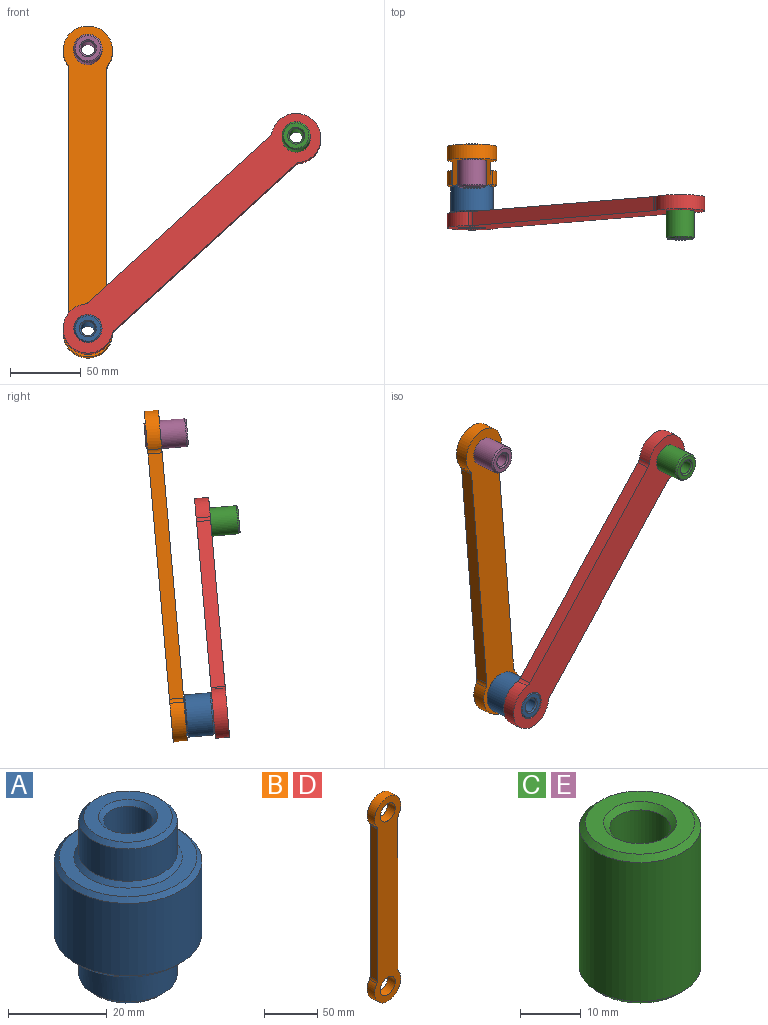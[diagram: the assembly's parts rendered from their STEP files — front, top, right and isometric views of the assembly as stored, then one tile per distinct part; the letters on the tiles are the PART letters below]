
ASSEMBLY  parts=5 mates=4
PART A: 16 faces, bbox 30x30x40 mm
  f0: cylinder r=15mm len=30mm, axis (0,0,-1), area 1696.5mm2, adj f11,f13
  f1: plane 28x28mm, normal (0,0,1), area 235.6mm2, adj f12,f13
  f2: plane 28x28mm, normal (0,0,-1), area 235.6mm2, adj f10,f11
  f3: cylinder r=10mm len=20mm, axis (0,0,-1), area 502.7mm2, adj f12,f15
  f4: plane 18x18mm, normal (0,0,1), area 141.4mm2, adj f14,f15
  f5: cylinder r=10mm len=20mm, axis (0,0,1), area 502.7mm2, adj f9,f10
  f6: plane 18x18mm, normal (0,0,-1), area 141.4mm2, adj f8,f9
  f7: cylinder r=5mm len=38mm, axis (0,0,1), area 1193.8mm2, adj f8,f14
  f8: cone r=6mm half-angle=45deg, axis (0,0,-1), area 48.9mm2, adj f6,f7
  f9: cone r=9mm half-angle=45deg, axis (0,0,1), area 84.4mm2, adj f5,f6
  f10: cone r=10mm half-angle=45deg, axis (0,0,1), area 93.3mm2, adj f2,f5
  f11: cone r=15mm half-angle=45deg, axis (0,0,1), area 128.8mm2, adj f0,f2
  f12: cone r=10mm half-angle=45deg, axis (0,0,-1), area 93.3mm2, adj f1,f3
  f13: cone r=14mm half-angle=45deg, axis (0,0,-1), area 128.8mm2, adj f0,f1
  f14: cone r=5mm half-angle=45deg, axis (0,0,1), area 48.9mm2, adj f4,f7
  f15: cone r=9mm half-angle=45deg, axis (0,0,-1), area 84.4mm2, adj f3,f4
PART B: 12 faces, bbox 35x10x235 mm
  f0: cylinder r=5mm len=10mm, axis (0,1,0), area 30.6mm2, adj f1,f9,f10,f11
  f1: cylinder r=17.5mm len=35mm, axis (0,1,0), area 763.6mm2, adj f0,f2,f10,f11
  f2: cylinder r=5mm len=10mm, axis (0,1,0), area 30.6mm2, adj f1,f3,f10,f11
  f3: plane 174.18x10mm, normal (-1,0,0), area 1741.8mm2, adj f2,f4,f10,f11
  f4: cylinder r=5mm len=10mm, axis (0,1,0), area 30.6mm2, adj f3,f5,f10,f11
  f5: cylinder r=17.5mm len=35mm, axis (0,1,0), area 763.6mm2, adj f4,f6,f10,f11
  f6: cylinder r=5mm len=10mm, axis (0,1,0), area 30.6mm2, adj f5,f9,f10,f11
  f7: cylinder r=10mm len=20mm, axis (0,1,0), area 628.3mm2, adj f10,f11
  f8: cylinder r=10mm len=20mm, axis (0,1,0), area 628.3mm2, adj f10,f11
  f9: plane 174.18x10mm, normal (1,0,0), area 1741.8mm2, adj f0,f6,f10,f11
  f10: plane 235x35mm, normal (0,-1,0), area 5831.3mm2, adj f0,f1,f2,f3,f4,f5,f6,f7
  f11: plane 235x35mm, normal (0,1,0), area 5831.3mm2, adj f0,f1,f2,f3,f4,f5,f6,f7
PART C: 8 faces, bbox 20x20x30 mm
  f0: cylinder r=10mm len=28mm, axis (0,0,-1), area 1759.3mm2, adj f6,f7
  f1: plane 18x18mm, normal (0,0,1), area 141.4mm2, adj f5,f6
  f2: plane 18x18mm, normal (0,0,-1), area 141.4mm2, adj f4,f7
  f3: cylinder r=5mm len=28mm, axis (0,0,-1), area 879.6mm2, adj f4,f5
  f4: cone r=5mm half-angle=45deg, axis (0,0,-1), area 48.9mm2, adj f2,f3
  f5: cone r=6mm half-angle=45deg, axis (0,0,1), area 48.9mm2, adj f1,f3
  f6: cone r=9mm half-angle=45deg, axis (0,0,-1), area 84.4mm2, adj f0,f1
  f7: cone r=10mm half-angle=45deg, axis (0,0,1), area 84.4mm2, adj f0,f2
PART D: same geometry as B
PART E: same geometry as C
PLACE A rot(axis=(-1,0,0),95deg) t=(48.86,-32.99,-9.76)mm
PLACE B rot(axis=(-1,0,0),5deg) t=(48.86,-13.06,-11.5)mm fixed
PLACE C rot(axis=(-0.39,-0.68,-0.62),140.4deg) t=(196.21,-61.05,128.45)mm
PLACE D rot(axis=(-0.1,0.99,-0.04),47.7deg) t=(48.86,-42.95,-8.89)mm
PLACE E rot(axis=(0.56,0.56,-0.61),117.2deg) t=(48.86,5.36,187.65)mm
MATE revolute D.f5 <-> A.f0  axis (0,-1,0.09) through (48.86,-52.91,-8.02)mm
MATE cylindrical D.f8 <-> C.f0  axis (0,1,-0.09) through (196.21,-41.12,126.7)mm
MATE fastened B.f5 <-> A.f0  axis (0,-1,0.09) through (48.86,-23.03,-10.63)mm
MATE fastened E.f0 <-> B.f8  axis (0,-1,0.09) through (48.86,4.37,187.73)mm
